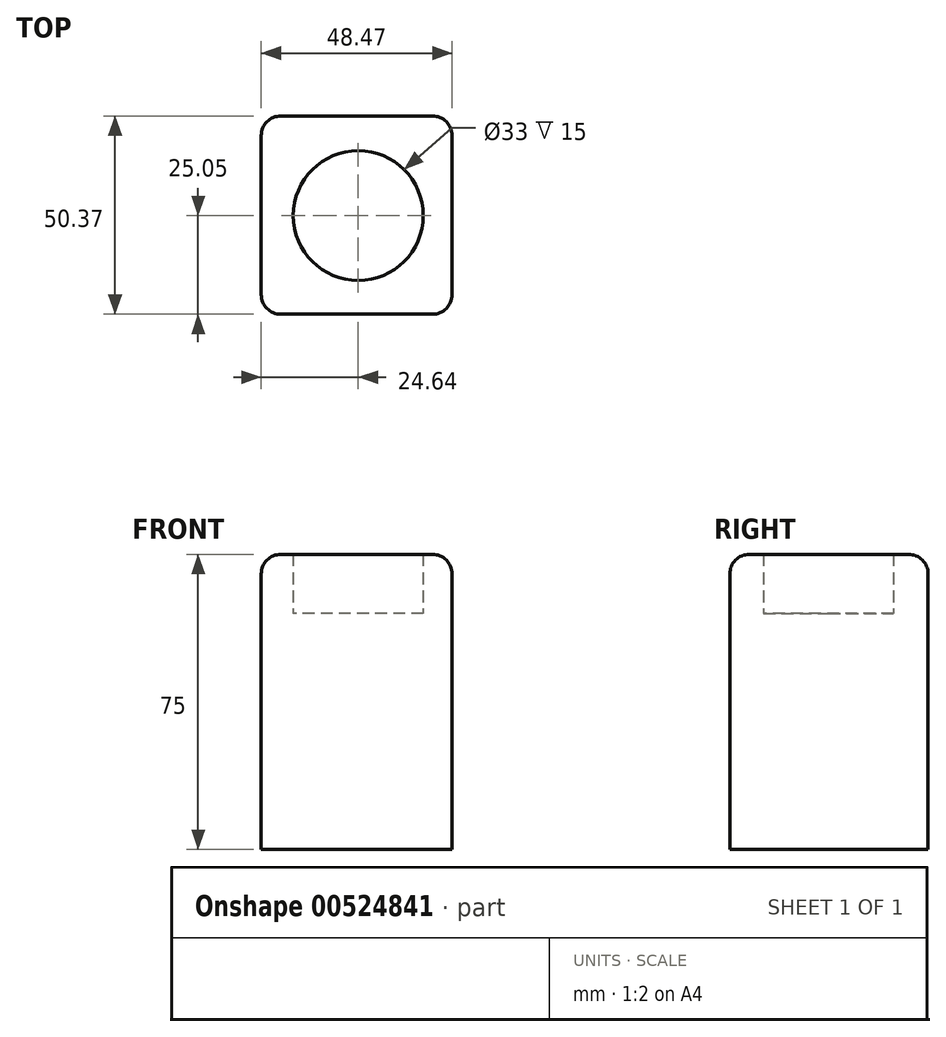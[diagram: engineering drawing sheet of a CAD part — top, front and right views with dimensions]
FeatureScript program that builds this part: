
annotation { "Feature Type Name" : "Feature", "Feature Type Description" : "" }
export const myFeature = defineFeature(function(context is Context, id is Id, definition is map)
    precondition{}
    {
        {
            var Q0;
            Q0=qCreatedBy(makeId("Top.planeOp"),FACE);
            var sketch = newSketch(context, id + "F0", { "sketchPlane" : qUnion([Q0])});
            skCircle(sketch, "E0", {"center": v(0, 0) * mm, "radius": 16.5 * mm});
            skLineSegment(sketch, "E1.bottom", {"start": v(-24.64, -25.05) * mm, "end": v(23.83, -25.05) * mm});
            skLineSegment(sketch, "E1.top", {"start": v(-24.64, 25.32) * mm, "end": v(23.83, 25.32) * mm});
            skLineSegment(sketch, "E1.left", {"start": v(-24.64, -25.05) * mm, "end": v(-24.64, 25.32) * mm});
            skLineSegment(sketch, "E1.right", {"start": v(23.83, -25.05) * mm, "end": v(23.83, 25.32) * mm});
            skSolve(sketch);
        }
        {
            var Q0;
            Q0=makeQuery(id+"F0.imprint","IMPRINT",FACE,{"disambiguationData":[TD([[makeQuery(id+"F0.imprint","IMPRINT",EDGE,{"derivedFrom":sQuery(id+"F0.wireOp",EDGE,"E0")}),-1.0]])]});
            extrude(context, id + "F1", {"entities" : qUnion([Q0]), "depth" : 75 * mm, "offsetDistance" : 25 * mm});
        }
        {
            var Q0;
            Q0=makeQuery(id+"F0.imprint","IMPRINT",FACE,{"disambiguationData":[TD([[makeQuery(id+"F0.imprint","IMPRINT",EDGE,{"derivedFrom":sQuery(id+"F0.wireOp",EDGE,"E0")}),1.0]])]});
            extrude(context, id + "F2", {"entities" : qUnion([Q0]), "operationType" : NewBodyOperationType.ADD, "depth" : 60 * mm, "offsetDistance" : 25 * mm});
        }
        {
            var Q0;
            Q0=makeQuery(id+"F1.opExtrude","SWEPT_EDGE",EDGE,{"disambiguationData":[OSD([sQuery(id+"F0.wireOp",EDGE,"E1.top"),sQuery(id+"F0.wireOp",EDGE,"E1.right")])]});
            var Q1;
            Q1=makeQuery(id+"F1.opExtrude","SWEPT_EDGE",EDGE,{"disambiguationData":[OSD([sQuery(id+"F0.wireOp",EDGE,"E1.top"),sQuery(id+"F0.wireOp",EDGE,"E1.left")])]});
            var Q2;
            Q2=makeQuery(id+"F1.opExtrude","SWEPT_EDGE",EDGE,{"disambiguationData":[OSD([sQuery(id+"F0.wireOp",EDGE,"E1.bottom"),sQuery(id+"F0.wireOp",EDGE,"E1.right")])]});
            var Q3;
            Q3=makeQuery(id+"F1.opExtrude","SWEPT_EDGE",EDGE,{"disambiguationData":[OSD([sQuery(id+"F0.wireOp",EDGE,"E1.bottom"),sQuery(id+"F0.wireOp",EDGE,"E1.left")])]});
            fillet(context, id + "F3", {"entities" : qUnion([Q0, Q1, Q2, Q3]), "radius" : 5 * mm, "tangentPropagation" : true, "allowEdgeOverflow" : false});
        }
        {
            var Q0;
            Q0=makeQuery(id+"F1.opExtrude","CAP_EDGE",EDGE,{"disambiguationData":[OSD([sQuery(id+"F0.wireOp",EDGE,"E1.top")])],"isStart":false});
            var Q1;
            Q1=makeQuery(id+"F1.opExtrude","CAP_EDGE",EDGE,{"disambiguationData":[OSD([sQuery(id+"F0.wireOp",EDGE,"E1.right")])],"isStart":false});
            var Q2;
            Q2=makeQuery(id+"F1.opExtrude","CAP_EDGE",EDGE,{"disambiguationData":[OSD([sQuery(id+"F0.wireOp",EDGE,"E1.bottom")])],"isStart":false});
            var Q3;
            Q3=makeQuery(id+"F1.opExtrude","CAP_EDGE",EDGE,{"disambiguationData":[OSD([sQuery(id+"F0.wireOp",EDGE,"E1.left")])],"isStart":false});
            fillet(context, id + "F4", {"entities" : qUnion([Q0, Q1, Q2, Q3]), "radius" : 5 * mm, "tangentPropagation" : true, "allowEdgeOverflow" : false});
        }
    });
